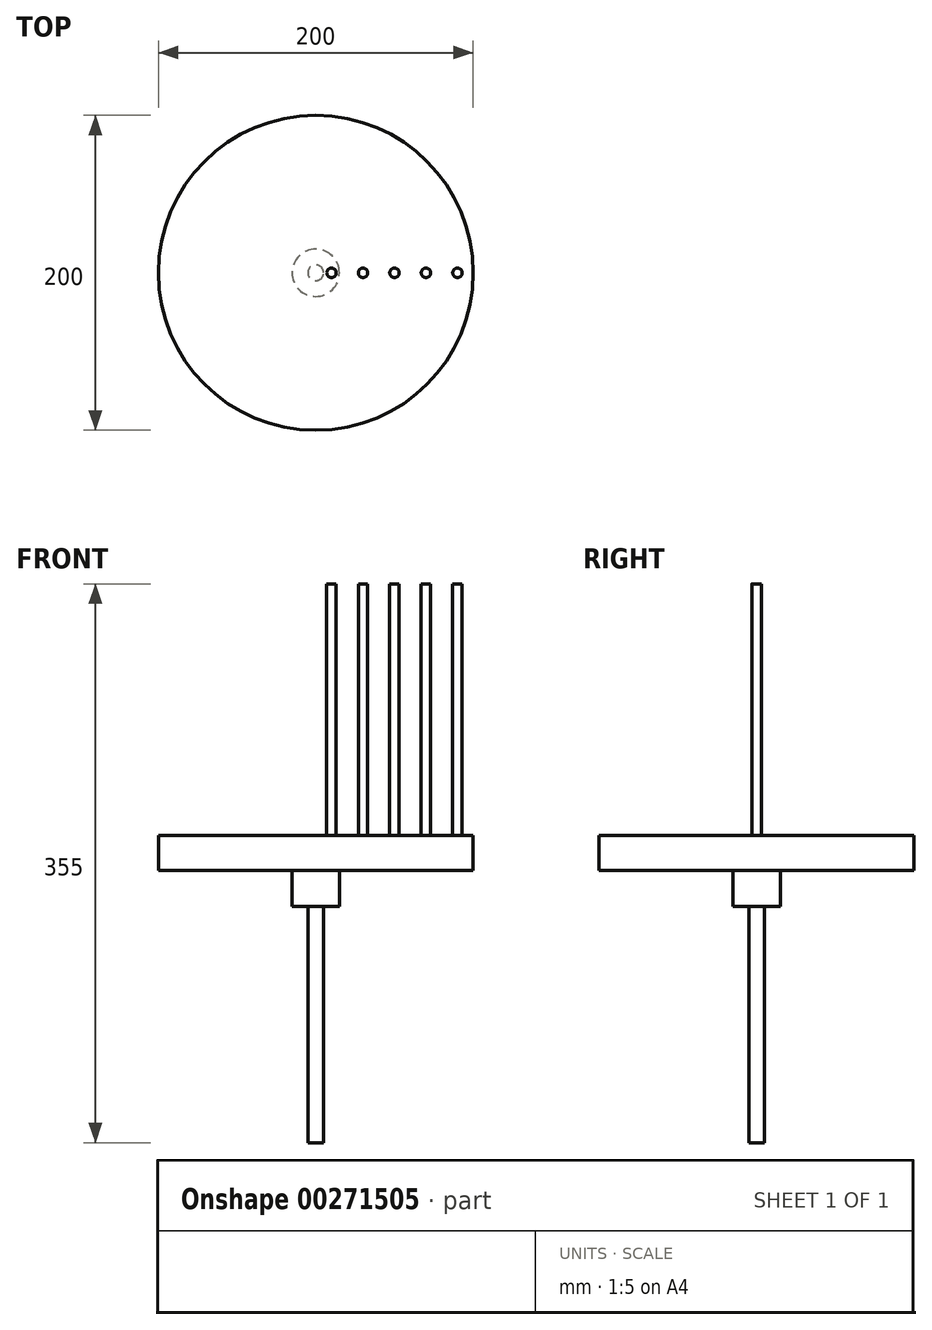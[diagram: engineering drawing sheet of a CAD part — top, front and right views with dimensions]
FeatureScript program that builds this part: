
annotation { "Feature Type Name" : "Feature", "Feature Type Description" : "" }
export const myFeature = defineFeature(function(context is Context, id is Id, definition is map)
    precondition{}
    {
        {
            var Q0;
            Q0=qCreatedBy(makeId("Top.planeOp"),FACE);
            var sketch = newSketch(context, id + "F0", { "sketchPlane" : qUnion([Q0])});
            skCircle(sketch, "E0", {"center": v(0, 0) * mm, "radius": 100 * mm});
            skSolve(sketch);
        }
        {
            var Q0;
            Q0=makeQuery(id+"F0.imprint","IMPRINT",FACE,{"disambiguationData":[TD([[makeQuery(id+"F0.imprint","IMPRINT",EDGE,{"derivedFrom":sQuery(id+"F0.wireOp",EDGE,"E0")}),1.0]])]});
            extrude(context, id + "F1", {"entities" : qUnion([Q0]), "depth" : 22 * mm});
        }
        {
            var Q0;
            Q0=makeQuery(id+"F1.opExtrude","CAP_FACE",FACE,{"disambiguationData":[OSD([sQuery(id+"F0.wireOp",EDGE,"E0")])],"isStart":false});
            var sketch = newSketch(context, id + "F2", { "sketchPlane" : qUnion([Q0])});
            skCircle(sketch, "E1", {"center": v(10, 0) * mm, "radius": 3 * mm});
            skCircle(sketch, "E2.1.0.0", {"center": v(30, 0) * mm, "radius": 3 * mm});
            skCircle(sketch, "E2.2.0.0", {"center": v(50, 0) * mm, "radius": 3 * mm});
            skCircle(sketch, "E2.3.0.0", {"center": v(70, 0) * mm, "radius": 3 * mm});
            skCircle(sketch, "E2.4.0.0", {"center": v(90, 0) * mm, "radius": 3 * mm});
            skLineSegment(sketch, "E2.direction1", {"start": v(10, 0) * mm, "end": v(30, 0) * mm, "construction": true});
            skSolve(sketch);
        }
        {
            var Q0;
            Q0=makeQuery(id+"F2.imprint","IMPRINT",FACE,{"disambiguationData":[TD([[makeQuery(id+"F2.imprint","IMPRINT",EDGE,{"derivedFrom":sQuery(id+"F2.wireOp",EDGE,"E1")}),1.0]])]});
            var Q1;
            Q1=makeQuery(id+"F2.imprint","IMPRINT",FACE,{"disambiguationData":[TD([[makeQuery(id+"F2.imprint","IMPRINT",EDGE,{"derivedFrom":sQuery(id+"F2.wireOp",EDGE,"E2.1.0.0")}),1.0]])]});
            var Q2;
            Q2=makeQuery(id+"F2.imprint","IMPRINT",FACE,{"disambiguationData":[TD([[makeQuery(id+"F2.imprint","IMPRINT",EDGE,{"derivedFrom":sQuery(id+"F2.wireOp",EDGE,"E2.2.0.0")}),1.0]])]});
            var Q3;
            Q3=makeQuery(id+"F2.imprint","IMPRINT",FACE,{"disambiguationData":[TD([[makeQuery(id+"F2.imprint","IMPRINT",EDGE,{"derivedFrom":sQuery(id+"F2.wireOp",EDGE,"E2.3.0.0")}),1.0]])]});
            var Q4;
            Q4=makeQuery(id+"F2.imprint","IMPRINT",FACE,{"disambiguationData":[TD([[makeQuery(id+"F2.imprint","IMPRINT",EDGE,{"derivedFrom":sQuery(id+"F2.wireOp",EDGE,"E2.4.0.0")}),1.0]])]});
            extrude(context, id + "F3", {"entities" : qUnion([Q0, Q1, Q2, Q3, Q4]), "operationType" : NewBodyOperationType.ADD, "depth" : 160 * mm});
        }
        {
            var Q0;
            Q0=makeQuery(id+"F0.imprint","IMPRINT",FACE,{"disambiguationData":[TD([[makeQuery(id+"F0.imprint","IMPRINT",EDGE,{"derivedFrom":sQuery(id+"F0.wireOp",EDGE,"E0")}),1.0]])]});
            var sketch = newSketch(context, id + "F4", { "sketchPlane" : qUnion([Q0])});
            skCircle(sketch, "E3", {"center": v(0, 0) * mm, "radius": 15 * mm});
            skSolve(sketch);
        }
        {
            var Q0;
            Q0=makeQuery(id+"F4.imprint","IMPRINT",FACE,{"disambiguationData":[TD([[makeQuery(id+"F4.imprint","IMPRINT",EDGE,{"derivedFrom":sQuery(id+"F4.wireOp",EDGE,"E3")}),1.0]])]});
            extrude(context, id + "F5", {"entities" : qUnion([Q0]), "operationType" : NewBodyOperationType.ADD, "oppositeDirection" : true, "depth" : 23 * mm});
        }
        {
            var Q0;
            Q0=makeQuery(id+"F5.opExtrude","CAP_FACE",FACE,{"disambiguationData":[OSD([sQuery(id+"F4.wireOp",EDGE,"E3")])],"isStart":false});
            var sketch = newSketch(context, id + "F6", { "sketchPlane" : qUnion([Q0])});
            skCircle(sketch, "E4.0", {"center": v(0, 0) * mm, "radius": 15 * mm});
            skCircle(sketch, "E5", {"center": v(0, 0) * mm, "radius": 5 * mm});
            skSolve(sketch);
        }
        {
            var Q0;
            Q0=makeQuery(id+"F6.imprint","IMPRINT",FACE,{"disambiguationData":[TD([[makeQuery(id+"F6.imprint","IMPRINT",EDGE,{"derivedFrom":sQuery(id+"F6.wireOp",EDGE,"E5")}),1.0]])]});
            extrude(context, id + "F7", {"entities" : qUnion([Q0]), "operationType" : NewBodyOperationType.ADD, "depth" : 150 * mm});
        }
    });
